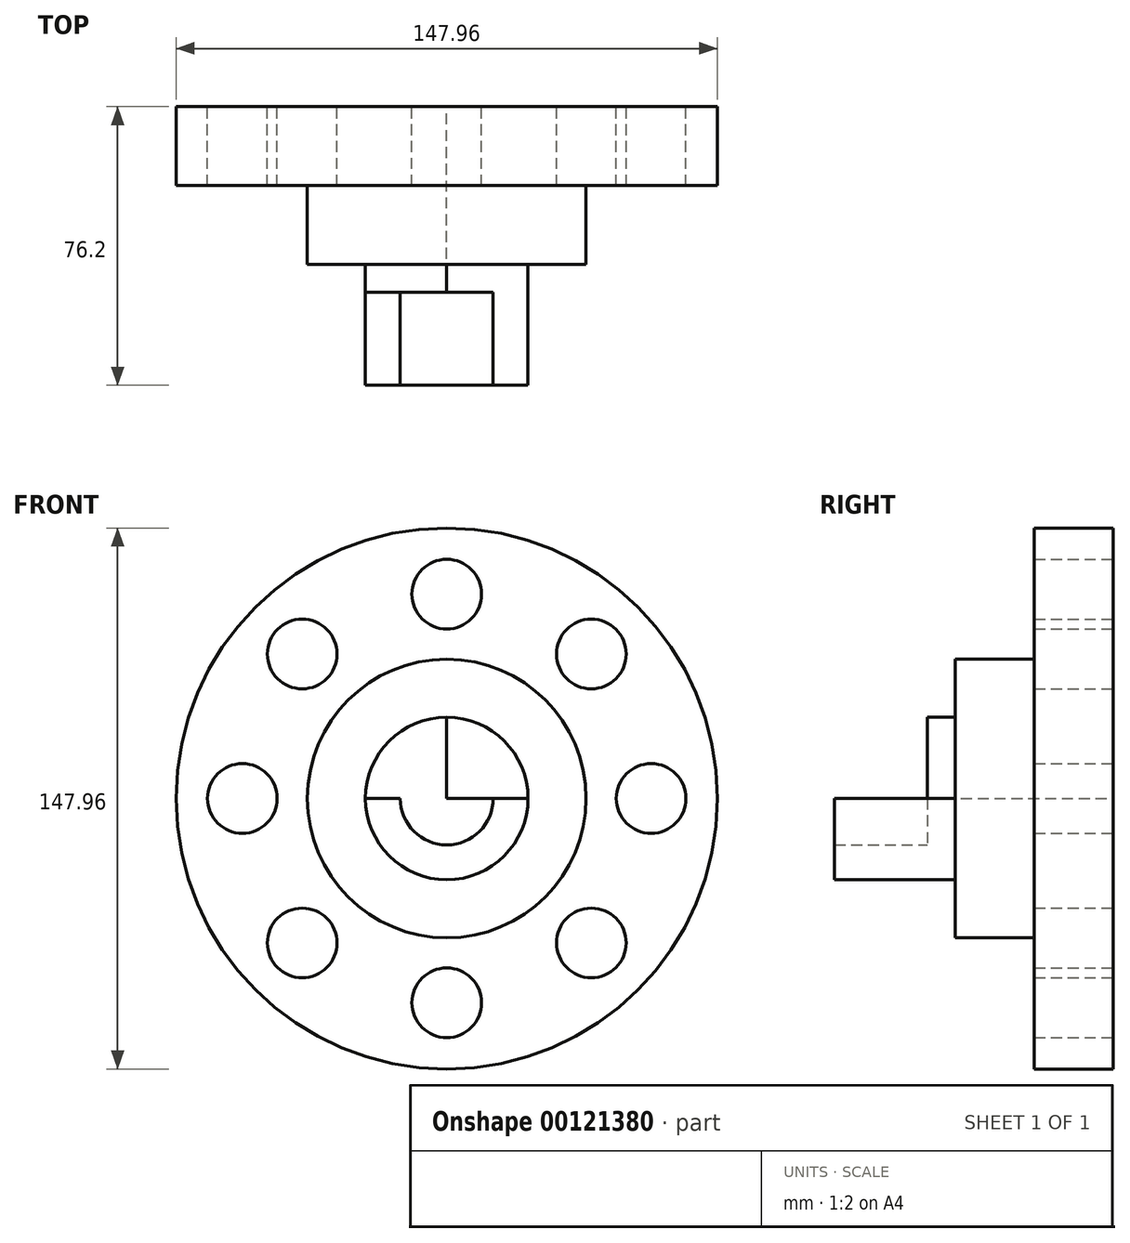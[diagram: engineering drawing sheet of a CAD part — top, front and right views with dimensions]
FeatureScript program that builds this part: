
annotation { "Feature Type Name" : "Feature", "Feature Type Description" : "" }
export const myFeature = defineFeature(function(context is Context, id is Id, definition is map)
    precondition{}
    {
        {
            var Q0;
            Q0=qCreatedBy(makeId("Front.planeOp"),FACE);
            var sketch = newSketch(context, id + "F0", { "sketchPlane" : qUnion([Q0])});
            skCircle(sketch, "E0", {"center": v(0, 0) * mm, "radius": 12.7 * mm});
            skCircle(sketch, "E1", {"center": v(0, 0) * mm, "radius": 22.23 * mm});
            skCircle(sketch, "E2", {"center": v(0, 0) * mm, "radius": 38.1 * mm});
            skCircle(sketch, "E3", {"center": v(0, 0) * mm, "radius": 55.88 * mm});
            skCircle(sketch, "E4", {"center": v(0, 0) * mm, "radius": 73.98 * mm});
            skCircle(sketch, "E5", {"center": v(0, 55.88) * mm, "radius": 9.53 * mm});
            skCircle(sketch, "E6.1.0", {"center": v(-39.51, 39.51) * mm, "radius": 9.53 * mm});
            skCircle(sketch, "E6.2.0", {"center": v(-55.88, 0) * mm, "radius": 9.53 * mm});
            skCircle(sketch, "E6.3.0", {"center": v(-39.51, -39.51) * mm, "radius": 9.53 * mm});
            skCircle(sketch, "E6.4.0", {"center": v(0, -55.88) * mm, "radius": 9.53 * mm});
            skCircle(sketch, "E6.5.0", {"center": v(39.51, -39.51) * mm, "radius": 9.53 * mm});
            skCircle(sketch, "E6.6.0", {"center": v(55.88, 0) * mm, "radius": 9.53 * mm});
            skCircle(sketch, "E6.7.0", {"center": v(39.51, 39.51) * mm, "radius": 9.53 * mm});
            skLineSegment(sketch, "E7", {"start": v(0, 55.88) * mm, "end": v(0, -55.88) * mm});
            skLineSegment(sketch, "E8", {"start": v(55.88, 0) * mm, "end": v(-55.88, 0) * mm});
            skLineSegment(sketch, "E9.bottom", {"start": v(3.17, -15.88) * mm, "end": v(-3.18, -15.88) * mm});
            skLineSegment(sketch, "E9.top", {"start": v(3.17, -9.53) * mm, "end": v(-3.18, -9.53) * mm});
            skLineSegment(sketch, "E9.left", {"start": v(3.17, -15.88) * mm, "end": v(3.17, -9.53) * mm});
            skLineSegment(sketch, "E9.right", {"start": v(-3.18, -15.88) * mm, "end": v(-3.18, -9.53) * mm});
            skPoint(sketch, "E9.middle", {"position": v(0, -12.7) * mm});
            skSolve(sketch);
        }
        {
            var Q0;
            Q0=qSketchRegion(id+"F0",true);
            var Q1;
            Q1=makeQuery(id+"F0.imprint","IMPRINT",FACE,{"disambiguationData":[TD([[makeQuery(id+"F0.imprint","IMPRINT",EDGE,{"derivedFrom":sQuery(id+"F0.wireOp",EDGE,"E2")}),-1.0]])]});
            extrude(context, id + "F1", {"entities" : qUnion([Q0, Q1]), "depth" : 21.59 * mm});
        }
        {
            var Q0;
            {var subQ0=sQuery(id+"F0.wireOp",EDGE,"E7");var subQ1=sQuery(id+"F0.wireOp",EDGE,"E1");var subQ2=makeQuery(id+"F0.imprint","INTERSECT",VERTEX,{"disambiguationData":[OD(0.0)],"derivedFrom":[subQ1,subQ0]});Q0=makeQuery(id+"F0.imprint","IMPRINT",FACE,{"disambiguationData":[TD([[makeQuery(id+"F0.imprint","IMPRINT",EDGE,{"disambiguationData":[TD([[subQ2,-1.0]])],"derivedFrom":subQ1}),-1.0]])]});}
            var Q1;
            {var subQ0=sQuery(id+"F0.wireOp",EDGE,"E8");var subQ1=sQuery(id+"F0.wireOp",EDGE,"E1");var subQ2=makeQuery(id+"F0.imprint","INTERSECT",VERTEX,{"disambiguationData":[OD(1.0)],"derivedFrom":[subQ1,subQ0]});Q1=makeQuery(id+"F0.imprint","IMPRINT",FACE,{"disambiguationData":[TD([[makeQuery(id+"F0.imprint","IMPRINT",EDGE,{"disambiguationData":[TD([[subQ2,-1.0]])],"derivedFrom":subQ1}),-1.0]])]});}
            var Q2;
            {var subQ0=sQuery(id+"F0.wireOp",EDGE,"E8");var subQ1=sQuery(id+"F0.wireOp",EDGE,"E1");var subQ2=makeQuery(id+"F0.imprint","INTERSECT",VERTEX,{"disambiguationData":[OD(0.0)],"derivedFrom":[subQ1,subQ0]});Q2=makeQuery(id+"F0.imprint","IMPRINT",FACE,{"disambiguationData":[TD([[makeQuery(id+"F0.imprint","IMPRINT",EDGE,{"disambiguationData":[TD([[subQ2,1.0]])],"derivedFrom":subQ1}),-1.0]])]});}
            var Q3;
            {var subQ0=sQuery(id+"F0.wireOp",EDGE,"E7");var subQ1=sQuery(id+"F0.wireOp",EDGE,"E1");var subQ2=makeQuery(id+"F0.imprint","INTERSECT",VERTEX,{"disambiguationData":[OD(0.0)],"derivedFrom":[subQ1,subQ0]});Q3=makeQuery(id+"F0.imprint","IMPRINT",FACE,{"disambiguationData":[TD([[makeQuery(id+"F0.imprint","IMPRINT",EDGE,{"disambiguationData":[TD([[subQ2,1.0]])],"derivedFrom":subQ1}),-1.0]])]});}
            extrude(context, id + "F2", {"entities" : qUnion([Q0, Q1, Q2, Q3]), "operationType" : NewBodyOperationType.ADD, "depth" : 43.18 * mm});
        }
        {
            var Q0;
            {var subQ0=sQuery(id+"F0.wireOp",EDGE,"E7");var subQ1=sQuery(id+"F0.wireOp",EDGE,"E0");var subQ2=makeQuery(id+"F0.imprint","INTERSECT",VERTEX,{"disambiguationData":[OD(0.0)],"derivedFrom":[subQ1,subQ0]});Q0=makeQuery(id+"F0.imprint","IMPRINT",FACE,{"disambiguationData":[TD([[makeQuery(id+"F0.imprint","IMPRINT",EDGE,{"disambiguationData":[TD([[subQ2,-1.0]])],"derivedFrom":subQ1}),-1.0]])]});}
            var Q1;
            {var subQ0=sQuery(id+"F0.wireOp",EDGE,"E7");var subQ1=sQuery(id+"F0.wireOp",EDGE,"E0");var subQ2=makeQuery(id+"F0.imprint","INTERSECT",VERTEX,{"disambiguationData":[OD(0.0)],"derivedFrom":[subQ1,subQ0]});Q1=makeQuery(id+"F0.imprint","IMPRINT",FACE,{"disambiguationData":[TD([[makeQuery(id+"F0.imprint","IMPRINT",EDGE,{"disambiguationData":[TD([[subQ2,1.0]])],"derivedFrom":subQ1}),-1.0]])]});}
            var Q2;
            {var subQ0=sQuery(id+"F0.wireOp",EDGE,"E8");var subQ1=sQuery(id+"F0.wireOp",EDGE,"E0");var subQ2=makeQuery(id+"F0.imprint","INTERSECT",VERTEX,{"disambiguationData":[OD(0.0)],"derivedFrom":[subQ1,subQ0]});Q2=makeQuery(id+"F0.imprint","IMPRINT",FACE,{"disambiguationData":[TD([[makeQuery(id+"F0.imprint","IMPRINT",EDGE,{"disambiguationData":[TD([[subQ2,1.0]])],"derivedFrom":subQ1}),-1.0]])]});}
            var Q3;
            {var subQ0=sQuery(id+"F0.wireOp",EDGE,"E8");var subQ1=sQuery(id+"F0.wireOp",EDGE,"E0");var subQ2=makeQuery(id+"F0.imprint","INTERSECT",VERTEX,{"disambiguationData":[OD(1.0)],"derivedFrom":[subQ1,subQ0]});Q3=makeQuery(id+"F0.imprint","IMPRINT",FACE,{"disambiguationData":[TD([[makeQuery(id+"F0.imprint","IMPRINT",EDGE,{"disambiguationData":[TD([[subQ2,-1.0]])],"derivedFrom":subQ1}),-1.0]])]});}
            extrude(context, id + "F3", {"entities" : qUnion([Q0, Q1, Q2, Q3]), "operationType" : NewBodyOperationType.ADD, "depth" : 76.2 * mm});
        }
        {
            var Q0;
            {var subQ5=sQuery(id+"F0.wireOp",EDGE,"E8");var subQ6=sQuery(id+"F0.wireOp",EDGE,"E0");var subQ7=makeQuery(id+"F0.imprint","INTERSECT",VERTEX,{"disambiguationData":[OD(0.0)],"derivedFrom":[subQ6,subQ5]});Q0=makeQuery(id+"F0.imprint","IMPRINT",FACE,{"disambiguationData":[TD([[makeQuery(id+"F0.imprint","IMPRINT",EDGE,{"disambiguationData":[TD([[subQ7,1.0]])],"derivedFrom":subQ6}),1.0]])]});}
            var Q1;
            {var subQ5=sQuery(id+"F0.wireOp",EDGE,"E8");var subQ6=sQuery(id+"F0.wireOp",EDGE,"E0");var subQ7=makeQuery(id+"F0.imprint","INTERSECT",VERTEX,{"disambiguationData":[OD(1.0)],"derivedFrom":[subQ6,subQ5]});Q1=makeQuery(id+"F0.imprint","IMPRINT",FACE,{"disambiguationData":[TD([[makeQuery(id+"F0.imprint","IMPRINT",EDGE,{"disambiguationData":[TD([[subQ7,-1.0]])],"derivedFrom":subQ6}),1.0]])]});}
            var Q2;
            {var subQ0=sQuery(id+"F0.wireOp",EDGE,"E7");var subQ1=sQuery(id+"F0.wireOp",EDGE,"E0");var subQ2=makeQuery(id+"F0.imprint","INTERSECT",VERTEX,{"disambiguationData":[OD(0.0)],"derivedFrom":[subQ1,subQ0]});Q2=makeQuery(id+"F0.imprint","IMPRINT",FACE,{"disambiguationData":[TD([[makeQuery(id+"F0.imprint","IMPRINT",EDGE,{"disambiguationData":[TD([[subQ2,-1.0]])],"derivedFrom":subQ1}),1.0]])]});}
            var Q3;
            {var subQ0=sQuery(id+"F0.wireOp",EDGE,"E7");var subQ1=sQuery(id+"F0.wireOp",EDGE,"E0");var subQ2=makeQuery(id+"F0.imprint","INTERSECT",VERTEX,{"disambiguationData":[OD(0.0)],"derivedFrom":[subQ1,subQ0]});Q3=makeQuery(id+"F0.imprint","IMPRINT",FACE,{"disambiguationData":[TD([[makeQuery(id+"F0.imprint","IMPRINT",EDGE,{"disambiguationData":[TD([[subQ2,1.0]])],"derivedFrom":subQ1}),1.0]])]});}
            var Q4;
            {var subQ0=sQuery(id+"F0.wireOp",EDGE,"E9.right");var subQ1=sQuery(id+"F0.wireOp",EDGE,"E0");var subQ2=makeQuery(id+"F0.imprint","INTERSECT",VERTEX,{"derivedFrom":[subQ1,subQ0]});Q4=makeQuery(id+"F0.imprint","IMPRINT",FACE,{"disambiguationData":[TD([[makeQuery(id+"F0.imprint","IMPRINT",EDGE,{"disambiguationData":[TD([[subQ2,-1.0]])],"derivedFrom":subQ1}),-1.0]])]});}
            var Q5;
            {var subQ0=sQuery(id+"F0.wireOp",EDGE,"E7");var subQ1=sQuery(id+"F0.wireOp",EDGE,"E0");var subQ2=makeQuery(id+"F0.imprint","INTERSECT",VERTEX,{"disambiguationData":[OD(1.0)],"derivedFrom":[subQ1,subQ0]});Q5=makeQuery(id+"F0.imprint","IMPRINT",FACE,{"disambiguationData":[TD([[makeQuery(id+"F0.imprint","IMPRINT",EDGE,{"disambiguationData":[TD([[subQ2,-1.0]])],"derivedFrom":subQ1}),1.0]])]});}
            var Q6;
            {var subQ0=sQuery(id+"F0.wireOp",EDGE,"E7");var subQ1=sQuery(id+"F0.wireOp",EDGE,"E0");var subQ2=makeQuery(id+"F0.imprint","INTERSECT",VERTEX,{"disambiguationData":[OD(1.0)],"derivedFrom":[subQ1,subQ0]});Q6=makeQuery(id+"F0.imprint","IMPRINT",FACE,{"disambiguationData":[TD([[makeQuery(id+"F0.imprint","IMPRINT",EDGE,{"disambiguationData":[TD([[subQ2,-1.0]])],"derivedFrom":subQ1}),-1.0]])]});}
            var Q7;
            {var subQ0=sQuery(id+"F0.wireOp",EDGE,"E9.right");var subQ1=sQuery(id+"F0.wireOp",EDGE,"E0");var subQ2=makeQuery(id+"F0.imprint","INTERSECT",VERTEX,{"derivedFrom":[subQ1,subQ0]});Q7=makeQuery(id+"F0.imprint","IMPRINT",FACE,{"disambiguationData":[TD([[makeQuery(id+"F0.imprint","IMPRINT",EDGE,{"disambiguationData":[TD([[subQ2,-1.0]])],"derivedFrom":subQ1}),1.0]])]});}
            extrude(context, id + "F4", {"entities" : qUnion([Q0, Q1, Q2, Q3, Q4, Q5, Q6, Q7]), "operationType" : NewBodyOperationType.ADD, "depth" : 50.8 * mm});
        }
    });
